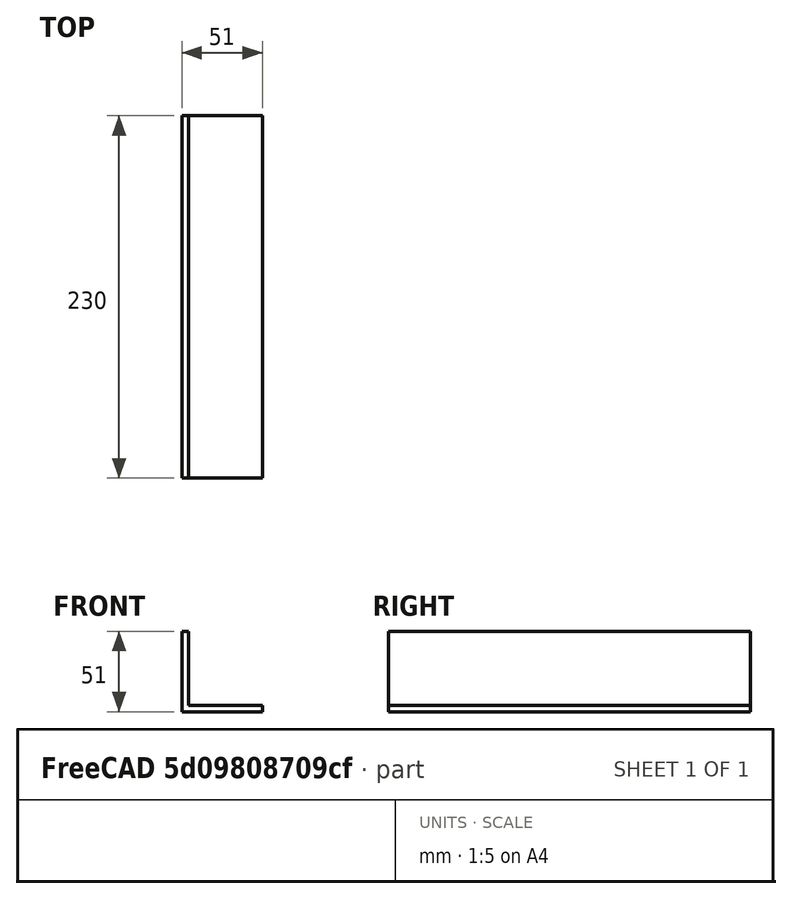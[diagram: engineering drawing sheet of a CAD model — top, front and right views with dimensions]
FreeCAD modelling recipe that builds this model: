
FCSTD DOCUMENT  (FreeCAD 0.15R4671 (Git))
Label: MainUpperFront
License: All rights reserved
LicenseURL: http://en.wikipedia.org/wiki/All_rights_reserved
objects: Sketcher::SketchObject×1, PartDesign::Pad×1
note: 3 computed .brp shape members not serialized (recipe doc carries the construction recipe); baked Part::Feature solids carry a one-line shape summary decoded from their .brp

FEATURE [Sketcher::SketchObject] Sketch
  Placement = pos=(0,0,0) rot=(1,0,0;1.5708rad)
  sketch-geometry (6):
    g0: LineSegment StartX=0 StartY=51 StartZ=0 EndX=0 EndY=0 EndZ=0
    g1: LineSegment StartX=0 StartY=0 StartZ=0 EndX=51 EndY=0 EndZ=0
    g2: LineSegment StartX=51 StartY=0 StartZ=0 EndX=51 EndY=4 EndZ=0
    g3: LineSegment StartX=51 StartY=4 StartZ=0 EndX=4 EndY=4 EndZ=0
    g4: LineSegment StartX=4 StartY=4 StartZ=0 EndX=4 EndY=51 EndZ=0
    g5: LineSegment StartX=4 StartY=51 StartZ=0 EndX=0 EndY=51 EndZ=0
  constraints (17):
    c: PointOnObject(g0,g-2)
    c: Coincident(g0,g-1)
    c: Coincident(g0,g1)
    c: Horizontal(g1)
    c: Coincident(g1,g2)
    c: Coincident(g2,g3)
    c: Horizontal(g3)
    c: Coincident(g3,g4)
    c: Coincident(g4,g5)
    c: Coincident(g5,g0)
    c: Horizontal(g5)
    c: Vertical(g2)
    c: Vertical(g4)
    c: DistanceY(g2) = 4
    c: DistanceX(g5) = -4
    c: DistanceY(g0) = -51
    c: DistanceX(g1) = 51
FEATURE [PartDesign::Pad] Pad
  Length = 230
  Length2 = 100
  Midplane = true
  Placement = pos=(0,0,0) rot=(1,0,0;1.5708rad)
  Sketch = -> Sketch
  Type = 0
